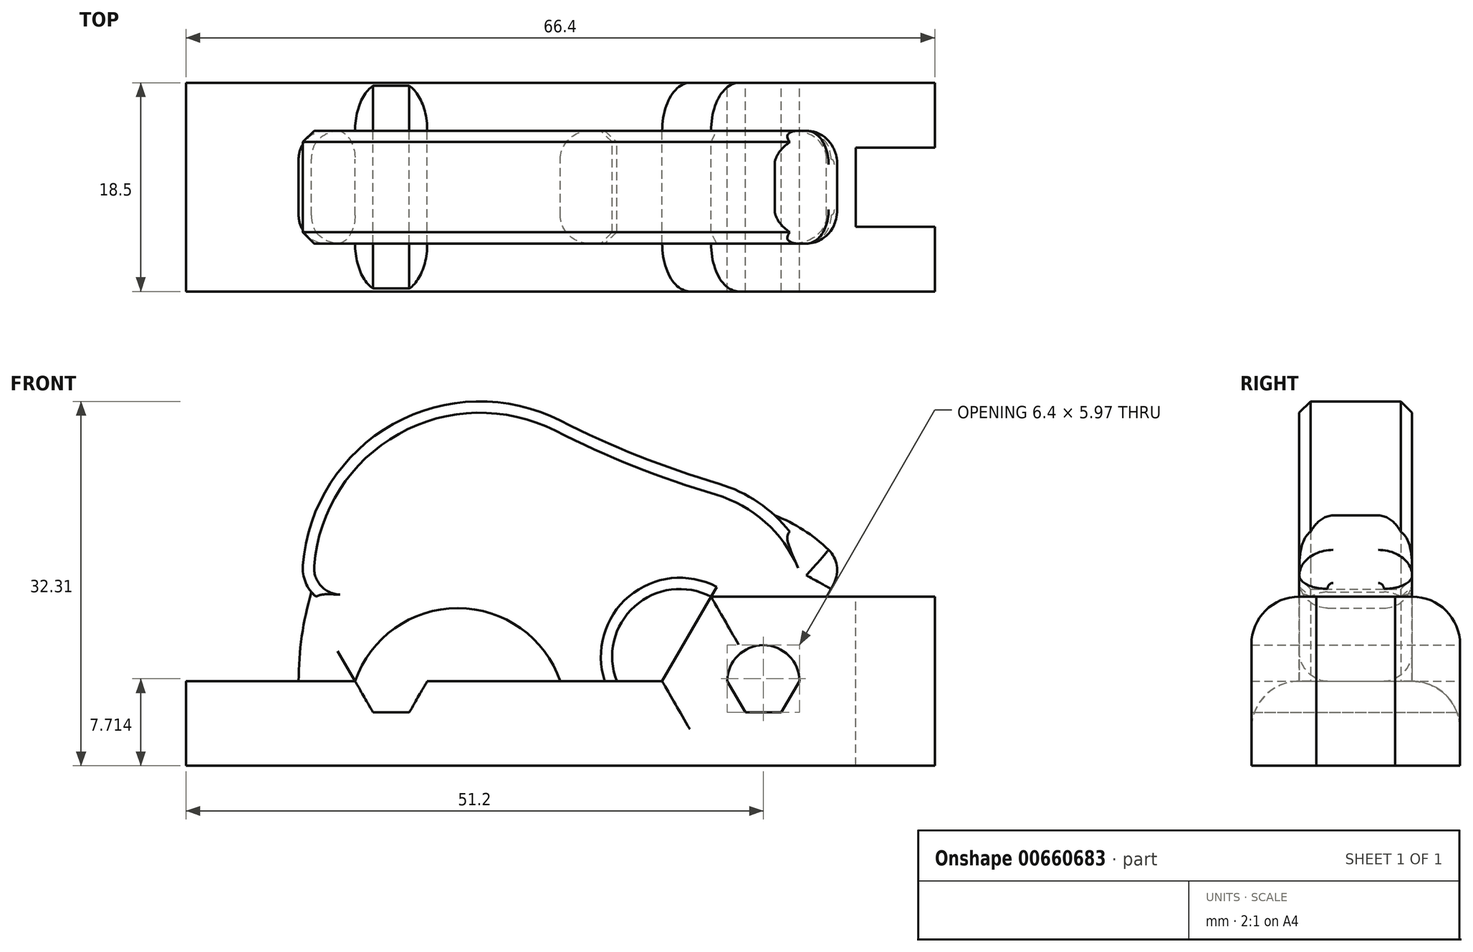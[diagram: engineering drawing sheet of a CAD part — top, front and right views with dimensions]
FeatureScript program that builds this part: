
annotation { "Feature Type Name" : "Feature", "Feature Type Description" : "" }
export const myFeature = defineFeature(function(context is Context, id is Id, definition is map)
    precondition{}
    {
        {
            var Q0;
            Q0=qCreatedBy(makeId("Front.planeOp"),FACE);
            var sketch = newSketch(context, id + "F0", { "sketchPlane" : qUnion([Q0])});
            skLineSegment(sketch, "E0", {"start": v(28.2, 0) * mm, "end": v(28.2, -7.5) * mm});
            skLineSegment(sketch, "E1", {"start": v(28.2, -7.5) * mm, "end": v(0, -7.5) * mm});
            skLineSegment(sketch, "E2.MirrorCS", {"start": v(-28.2, -7.5) * mm, "end": v(0, -7.5) * mm});
            skLineSegment(sketch, "E3.MirrorCS", {"start": v(-28.2, 0) * mm, "end": v(-28.2, -7.5) * mm, "construction": true});
            skLineSegment(sketch, "E4", {"start": v(28.2, 0) * mm, "end": v(28.2, 7.5) * mm});
            skLineSegment(sketch, "E5", {"start": v(28.2, 7.5) * mm, "end": v(13.2, 7.5) * mm});
            skArc(sketch, "E6", {"start": v(13.2, 7.5) * mm, "mid": v(-3.88, 14.68) * mm, "end": v(-15.18, 0) * mm, "construction": true});
            skLineSegment(sketch, "E7", {"start": v(-28.2, 0) * mm, "end": v(-23.2, 0) * mm});
            skLineSegment(sketch, "E8.trimOffspring", {"start": v(-16.8, 0) * mm, "end": v(-15.18, 0) * mm});
            skCircle(sketch, "E9", {"center": v(13, 0) * mm, "radius": 2.5 * mm, "construction": true});
            skPoint(sketch, "E9.centerSnap0", {"position": v(14.1, -7.5) * mm});
            skCircle(sketch, "E10.cCircle", {"center": v(-20, 0) * mm, "radius": 2.77 * mm, "construction": true});
            skLineSegment(sketch, "E10.0", {"start": v(-18.4, -2.77) * mm, "end": v(-21.6, -2.77) * mm});
            skLineSegment(sketch, "E10.1", {"start": v(-21.6, -2.77) * mm, "end": v(-23.2, 0) * mm});
            skLineSegment(sketch, "E10.2", {"start": v(-23.2, 0) * mm, "end": v(-21.6, 2.77) * mm, "construction": true});
            skLineSegment(sketch, "E10.3", {"start": v(-21.6, 2.77) * mm, "end": v(-18.4, 2.77) * mm, "construction": true});
            skLineSegment(sketch, "E10.4", {"start": v(-18.4, 2.77) * mm, "end": v(-16.8, 0) * mm, "construction": true});
            skLineSegment(sketch, "E10.5", {"start": v(-16.8, 0) * mm, "end": v(-18.4, -2.77) * mm});
            skPoint(sketch, "E10.0.midPoint", {"position": v(-20, -2.77) * mm});
            skCircle(sketch, "E11.cCircle", {"center": v(13, 0) * mm, "radius": 2.77 * mm, "construction": true});
            skLineSegment(sketch, "E11.0", {"start": v(11.4, 2.77) * mm, "end": v(14.6, 2.77) * mm, "construction": true});
            skLineSegment(sketch, "E11.1", {"start": v(14.6, 2.77) * mm, "end": v(16.2, 0) * mm, "construction": true});
            skLineSegment(sketch, "E11.2", {"start": v(16.2, 0) * mm, "end": v(14.6, -2.77) * mm});
            skLineSegment(sketch, "E11.3", {"start": v(14.6, -2.77) * mm, "end": v(11.4, -2.77) * mm});
            skLineSegment(sketch, "E11.4", {"start": v(11.4, -2.77) * mm, "end": v(9.8, 0) * mm});
            skLineSegment(sketch, "E11.5", {"start": v(9.8, 0) * mm, "end": v(11.4, 2.77) * mm, "construction": true});
            skPoint(sketch, "E11.0.midPoint", {"position": v(13, 2.77) * mm});
            skArc(sketch, "E12", {"start": v(9.8, 0) * mm, "mid": v(13, 3.2) * mm, "end": v(16.2, 0) * mm});
            skLineSegment(sketch, "E13", {"start": v(-15.18, 0) * mm, "end": v(4.03, 0) * mm});
            skLineSegment(sketch, "E14", {"start": v(4.03, 0) * mm, "end": v(8.36, 7.5) * mm});
            skLineSegment(sketch, "E15", {"start": v(8.36, 7.5) * mm, "end": v(13.2, 7.5) * mm});
            skLineSegment(sketch, "E16", {"start": v(-28.2, 0) * mm, "end": v(-38.2, 0) * mm});
            skLineSegment(sketch, "E17", {"start": v(-38.2, 0) * mm, "end": v(-38.2, -7.5) * mm});
            skLineSegment(sketch, "E18", {"start": v(-38.2, -7.5) * mm, "end": v(-28.2, -7.5) * mm});
            skSolve(sketch);
        }
        {
            var Q0;
            Q0=qSketchRegion(id+"F0",true);
            extrude(context, id + "F1", {"entities" : qUnion([Q0]), "endBound" : BoundingType.SYMMETRIC, "depth" : 18.5 * mm, "offsetDistance" : 25 * mm});
        }
        {
            var Q0;
            Q0=makeQuery(id+"F1.opExtrude","SWEPT_FACE",FACE,{"disambiguationData":[OSD([sQuery(id+"F0.wireOp",EDGE,"E5")])]});
            var sketch = newSketch(context, id + "F2", { "sketchPlane" : qUnion([Q0])});
            skLineSegment(sketch, "E19.bottom", {"start": v(28.2, -3.5) * mm, "end": v(21.2, -3.5) * mm});
            skLineSegment(sketch, "E19.top", {"start": v(28.2, 3.5) * mm, "end": v(21.2, 3.5) * mm});
            skLineSegment(sketch, "E19.left", {"start": v(28.2, -3.5) * mm, "end": v(28.2, 3.5) * mm});
            skLineSegment(sketch, "E19.right", {"start": v(21.2, -3.5) * mm, "end": v(21.2, 3.5) * mm});
            skPoint(sketch, "E19.middle", {"position": v(24.7, 0) * mm});
            skSolve(sketch);
        }
        {
            var Q0;
            Q0=qSketchRegion(id+"F2",true);
            extrude(context, id + "F3", {"entities" : qUnion([Q0]), "operationType" : NewBodyOperationType.REMOVE, "oppositeDirection" : true, "depth" : 25 * mm});
        }
        {
            var Q0;
            Q0=qCreatedBy(makeId("Front.planeOp"),FACE);
            var sketch = newSketch(context, id + "F4", { "sketchPlane" : qUnion([Q0])});
            skArc(sketch, "E20", {"start": v(-28.2, 0) * mm, "mid": v(-27.92, 4) * mm, "end": v(-27.07, 7.9) * mm});
            skLineSegment(sketch, "E21", {"start": v(18.6, 7.5) * mm, "end": v(8.36, 7.5) * mm});
            skLineSegment(sketch, "E22", {"start": v(0, 0) * mm, "end": v(-5, 0) * mm});
            skArc(sketch, "E23", {"start": v(-16.8, 0) * mm, "mid": v(-20, 3.2) * mm, "end": v(-23.2, 0) * mm, "construction": true});
            skLineSegment(sketch, "E24", {"start": v(-28.2, 0) * mm, "end": v(-23.2, 0) * mm});
            skLineSegment(sketch, "E25", {"start": v(-27.07, 7.9) * mm, "end": v(-27.07, 7.9) * mm});
            skArc(sketch, "E26", {"start": v(-27.82, 10.3) * mm, "mid": v(-27.68, 9.03) * mm, "end": v(-27.07, 7.9) * mm});
            skArc(sketch, "E27", {"start": v(-5, 23.1) * mm, "mid": v(-19.83, 22.8) * mm, "end": v(-27.82, 10.3) * mm});
            skArc(sketch, "E28", {"start": v(-5, 23.1) * mm, "mid": v(1.91, 19.99) * mm, "end": v(9.08, 17.5) * mm});
            skArc(sketch, "E29", {"start": v(14, 14.7) * mm, "mid": v(11.7, 16.38) * mm, "end": v(9.08, 17.5) * mm});
            skArc(sketch, "E30", {"start": v(20, 10.3) * mm, "mid": v(17.3, 12.9) * mm, "end": v(14, 14.7) * mm});
            skArc(sketch, "E31", {"start": v(18.6, 7.5) * mm, "mid": v(19.35, 8.88) * mm, "end": v(20, 10.3) * mm});
            skPoint(sketch, "E32.start.orphan", {"position": v(21.2, 7.5) * mm});
            skArc(sketch, "E33", {"start": v(8.36, 7.5) * mm, "mid": v(1.58, 6.64) * mm, "end": v(0, 0) * mm});
            skArc(sketch, "E34", {"start": v(-5, 0) * mm, "mid": v(-10, 5) * mm, "end": v(-15, 0) * mm, "construction": true});
            skLineSegment(sketch, "E35.trimOffspring", {"start": v(-15, 0) * mm, "end": v(-16.8, 0) * mm, "construction": true});
            skArc(sketch, "E36", {"start": v(-5, 0) * mm, "mid": v(-14.1, 6.48) * mm, "end": v(-23.2, 0) * mm});
            skSolve(sketch);
        }
        {
            var Q0;
            Q0=qSketchRegion(id+"F4",true);
            extrude(context, id + "F5", {"entities" : qUnion([Q0]), "operationType" : NewBodyOperationType.ADD, "endBound" : BoundingType.SYMMETRIC, "depth" : 10 * mm, "offsetDistance" : 25 * mm});
        }
        {
            var Q0;
            Q0=makeQuery(id+"F1.opExtrude","CAP_EDGE",EDGE,{"disambiguationData":[OSD([sQuery(id+"F0.wireOp",EDGE,"E8.trimOffspring"),sQuery(id+"F0.wireOp",EDGE,"E13")])],"isStart":false});
            var Q1;
            Q1=makeQuery(id+"F1.opExtrude","CAP_EDGE",EDGE,{"disambiguationData":[OSD([sQuery(id+"F0.wireOp",EDGE,"E8.trimOffspring"),sQuery(id+"F0.wireOp",EDGE,"E13")])],"isStart":true});
            var Q2;
            Q2=makeQuery(id+"F1.opExtrude","CAP_EDGE",EDGE,{"disambiguationData":[OSD([sQuery(id+"F0.wireOp",EDGE,"E14")])],"isStart":false});
            var Q3;
            Q3=makeQuery(id+"F1.opExtrude","CAP_EDGE",EDGE,{"disambiguationData":[OSD([sQuery(id+"F0.wireOp",EDGE,"E14")])],"isStart":true});
            var Q4;
            Q4=makeQuery(id+"F1.opExtrude","CAP_EDGE",EDGE,{"disambiguationData":[OSD([sQuery(id+"F0.wireOp",EDGE,"E5"),sQuery(id+"F0.wireOp",EDGE,"E15")])],"isStart":false});
            var Q5;
            Q5=makeQuery(id+"F1.opExtrude","CAP_EDGE",EDGE,{"disambiguationData":[OSD([sQuery(id+"F0.wireOp",EDGE,"E5"),sQuery(id+"F0.wireOp",EDGE,"E15")])],"isStart":true});
            fillet(context, id + "F6", {"entities" : qUnion([Q0, Q1, Q2, Q3, Q4, Q5]), "radius" : 4.25 * mm, "tangentPropagation" : true, "allowEdgeOverflow" : false});
        }
        {
            var Q0;
            Q0=makeQuery(id+"F5.opExtrude","CAP_EDGE",EDGE,{"disambiguationData":[OSD([sQuery(id+"F4.wireOp",EDGE,"E30")])],"isStart":false});
            var Q1;
            Q1=makeQuery(id+"F5.opExtrude","CAP_EDGE",EDGE,{"disambiguationData":[OSD([sQuery(id+"F4.wireOp",EDGE,"E30")])],"isStart":true});
            fillet(context, id + "F7", {"entities" : qUnion([Q0, Q1]), "radius" : 3 * mm, "tangentPropagation" : true, "allowEdgeOverflow" : false});
        }
        {
            var Q0;
            Q0=makeQuery(id+"F5.opExtrude","CAP_EDGE",EDGE,{"disambiguationData":[OSD([sQuery(id+"F4.wireOp",EDGE,"E36")])],"isStart":false});
            var Q1;
            Q1=makeQuery(id+"F5.opExtrude","CAP_EDGE",EDGE,{"disambiguationData":[OSD([sQuery(id+"F4.wireOp",EDGE,"E36")])],"isStart":true});
            fillet(context, id + "F8", {"entities" : qUnion([Q0, Q1]), "radius" : 2.5 * mm, "tangentPropagation" : true, "allowEdgeOverflow" : false});
        }
        {
            var Q0;
            Q0=makeQuery(id+"F5.opExtrude","CAP_EDGE",EDGE,{"disambiguationData":[OSD([sQuery(id+"F4.wireOp",EDGE,"E28")])],"isStart":false});
            var Q1;
            Q1=makeQuery(id+"F5.opExtrude","CAP_EDGE",EDGE,{"disambiguationData":[OSD([sQuery(id+"F4.wireOp",EDGE,"E27")])],"isStart":false});
            var Q2;
            Q2=makeQuery(id+"F5.opExtrude","CAP_EDGE",EDGE,{"disambiguationData":[OSD([sQuery(id+"F4.wireOp",EDGE,"E26")])],"isStart":false});
            var Q3;
            Q3=makeQuery(id+"F5.opExtrude","CAP_EDGE",EDGE,{"disambiguationData":[OSD([sQuery(id+"F4.wireOp",EDGE,"E28")])],"isStart":true});
            var Q4;
            Q4=makeQuery(id+"F5.opExtrude","CAP_EDGE",EDGE,{"disambiguationData":[OSD([sQuery(id+"F4.wireOp",EDGE,"E33")])],"isStart":false});
            var Q5;
            Q5=makeQuery(id+"F5.opExtrude","CAP_EDGE",EDGE,{"disambiguationData":[OSD([sQuery(id+"F4.wireOp",EDGE,"E33")])],"isStart":true});
            chamfer(context, id + "F9", {"entities" : qUnion([Q0, Q1, Q2, Q3, Q4, Q5]), "width" : 1 * mm, "tangentPropagation" : true});
        }
        {
            var Q0;
            Q0=makeQuery(id+"F5.opExtrude","CAP_EDGE",EDGE,{"disambiguationData":[OSD([sQuery(id+"F4.wireOp",EDGE,"E20")])],"isStart":false});
            var Q1;
            Q1=makeQuery(id+"F5.opExtrude","CAP_EDGE",EDGE,{"disambiguationData":[OSD([sQuery(id+"F4.wireOp",EDGE,"E20")])],"isStart":true});
            fillet(context, id + "F10", {"entities" : qUnion([Q0, Q1]), "radius" : 2.5 * mm, "tangentPropagation" : true, "allowEdgeOverflow" : false});
        }
        {
            var Q0;
            Q0=makeQuery(id+"F5.opExtrude","SWEPT_EDGE",EDGE,{"disambiguationData":[OSD([sQuery(id+"F4.wireOp",EDGE,"E30"),sQuery(id+"F4.wireOp",EDGE,"E31")])]});
            fillet(context, id + "F11", {"entities" : qUnion([Q0]), "radius" : 2.5 * mm, "tangentPropagation" : true, "allowEdgeOverflow" : false});
        }
    });
